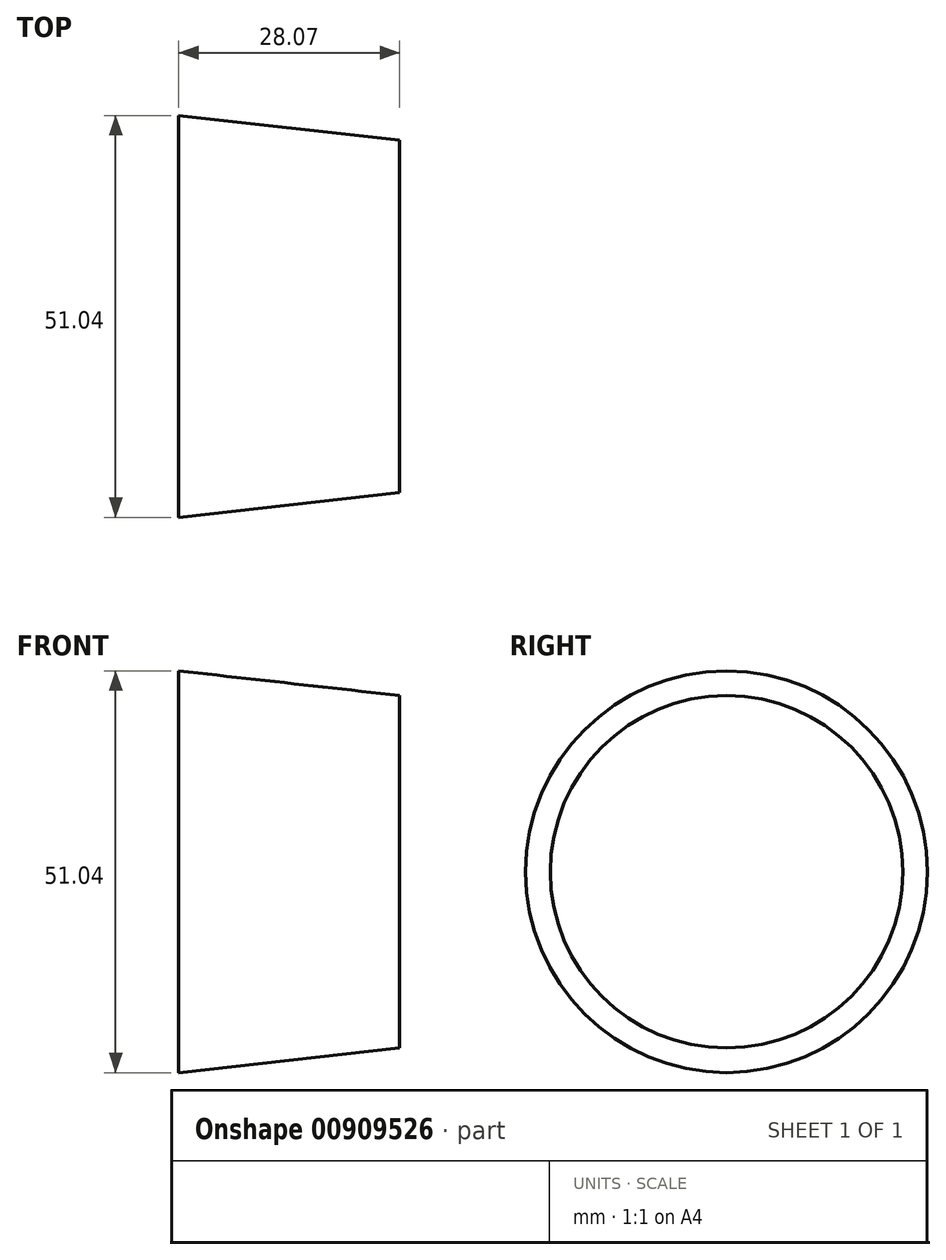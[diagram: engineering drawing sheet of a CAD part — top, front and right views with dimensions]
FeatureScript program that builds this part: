
annotation { "Feature Type Name" : "Feature", "Feature Type Description" : "" }
export const myFeature = defineFeature(function(context is Context, id is Id, definition is map)
    precondition{}
    {
        {
            var Q0;
            Q0=qCreatedBy(makeId("Top.planeOp"),FACE);
            var sketch = newSketch(context, id + "F0", { "sketchPlane" : qUnion([Q0])});
            skLineSegment(sketch, "E0", {"start": v(0, 0) * mm, "end": v(0, 25.52) * mm});
            skLineSegment(sketch, "E1", {"start": v(0, 25.52) * mm, "end": v(28.07, 25.52) * mm});
            skLineSegment(sketch, "E2", {"start": v(28.07, 25.52) * mm, "end": v(28.07, 3.13) * mm});
            skLineSegment(sketch, "E3", {"start": v(28.07, 3.13) * mm, "end": v(0, 0) * mm});
            skSolve(sketch);
        }
        {
            var Q0;
            Q0=makeQuery(id+"F0.imprint","IMPRINT",FACE,{"disambiguationData":[TD([[makeQuery(id+"F0.imprint","IMPRINT",EDGE,{"derivedFrom":sQuery(id+"F0.wireOp",EDGE,"E0")}),-1.0]])]});
            var Q1;
            Q1=sQuery(id+"F0.wireOp",EDGE,"E1");
            revolve(context, id + "F1", {"surfaceOperationType" : NewSurfaceOperationType.NEW, "entities" : qUnion([Q0]), "axis" : qUnion([Q1]), "revolveType" : RevolveType.FULL});
        }
    });
